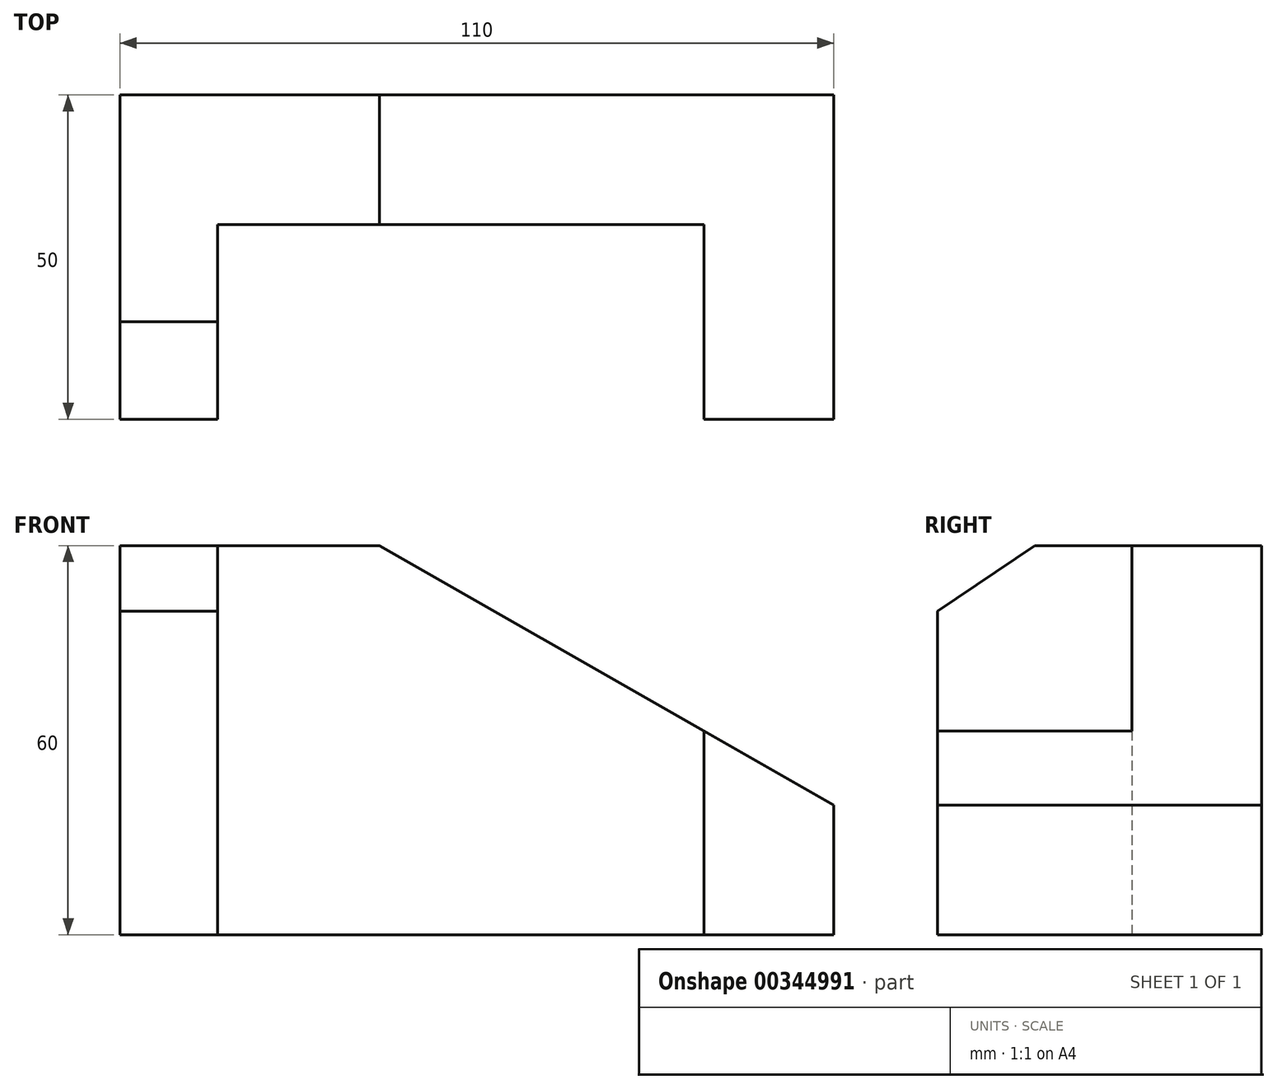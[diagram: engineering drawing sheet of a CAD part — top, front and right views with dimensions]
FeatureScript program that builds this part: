
annotation { "Feature Type Name" : "Feature", "Feature Type Description" : "" }
export const myFeature = defineFeature(function(context is Context, id is Id, definition is map)
    precondition{}
    {
        {
            var Q0;
            Q0=qCreatedBy(makeId("Top.planeOp"),FACE);
            var sketch = newSketch(context, id + "F0", { "sketchPlane" : qUnion([Q0])});
            skLineSegment(sketch, "E0.bottom", {"start": v(-55, 25) * mm, "end": v(55, 25) * mm});
            skLineSegment(sketch, "E0.top", {"start": v(-55, -25) * mm, "end": v(-40, -25) * mm});
            skLineSegment(sketch, "E0.left", {"start": v(-55, 25) * mm, "end": v(-55, -25) * mm});
            skLineSegment(sketch, "E0.right", {"start": v(55, 25) * mm, "end": v(55, -25) * mm});
            skPoint(sketch, "E0.middle", {"position": v(0, 0) * mm});
            skPoint(sketch, "E1", {"position": v(-15, 25) * mm});
            skPoint(sketch, "E2", {"position": v(-55, -5) * mm});
            skPoint(sketch, "E3", {"position": v(-40, 0) * mm});
            skPoint(sketch, "E4", {"position": v(35, -25) * mm});
            skLineSegment(sketch, "E5.trimOffspring", {"start": v(35, -25) * mm, "end": v(55, -25) * mm});
            skPoint(sketch, "E6", {"position": v(-55, 5) * mm});
            skLineSegment(sketch, "E7", {"start": v(-40, 5) * mm, "end": v(35, 5) * mm});
            skLineSegment(sketch, "E8", {"start": v(-40, -25) * mm, "end": v(-40, 5) * mm});
            skLineSegment(sketch, "E9", {"start": v(35, -25) * mm, "end": v(35, 5) * mm});
            skPoint(sketch, "E10.end.orphan", {"position": v(35, 0) * mm});
            skSolve(sketch);
        }
        {
            var Q0;
            Q0=makeQuery(id+"F0.imprint","IMPRINT",FACE,{"disambiguationData":[TD([[makeQuery(id+"F0.imprint","IMPRINT",EDGE,{"derivedFrom":sQuery(id+"F0.wireOp",EDGE,"E0.bottom")}),-1.0]])]});
            extrude(context, id + "F1", {"entities" : qUnion([Q0]), "depth" : 60 * mm});
        }
        {
            var Q0;
            Q0=makeQuery(id+"F1.opExtrude","SWEPT_FACE",FACE,{"disambiguationData":[OSD([sQuery(id+"F0.wireOp",EDGE,"E8")])]});
            var sketch = newSketch(context, id + "F2", { "sketchPlane" : qUnion([Q0])});
            skLineSegment(sketch, "E11.0", {"start": v(-25, 60) * mm, "end": v(5, 60) * mm});
            skLineSegment(sketch, "E11.1", {"start": v(-25, 60) * mm, "end": v(-25, 0) * mm});
            skLineSegment(sketch, "E11.2", {"start": v(5, 60) * mm, "end": v(5, 0) * mm});
            skLineSegment(sketch, "E11.3", {"start": v(-25, 0) * mm, "end": v(5, 0) * mm});
            skPoint(sketch, "E11.4", {"position": v(-10, 60) * mm});
            skPoint(sketch, "E12", {"position": v(-25, 49.9) * mm});
            skLineSegment(sketch, "E13", {"start": v(-25, 49.9) * mm, "end": v(-10, 60) * mm});
            skLineSegment(sketch, "E14", {"start": v(-25.07, 60.14) * mm, "end": v(-9.82, 60.17) * mm});
            skLineSegment(sketch, "E15", {"start": v(-25, 60) * mm, "end": v(-25, 49.9) * mm});
            skSolve(sketch);
        }
        {
            var Q0;
            {var subQ2=sQuery(id+"F2.wireOp",EDGE,"E13");Q0=makeQuery(id+"F2.imprint","IMPRINT",FACE,{"disambiguationData":[TD([[makeQuery(id+"F2.imprint","IMPRINT",EDGE,{"derivedFrom":subQ2}),1.0]])]});}
            extrude(context, id + "F3", {"entities" : qUnion([Q0]), "operationType" : NewBodyOperationType.REMOVE, "oppositeDirection" : true, "depth" : 15 * mm});
        }
        {
            var Q0;
            Q0=makeQuery(id+"F1.opExtrude","SWEPT_FACE",FACE,{"disambiguationData":[OSD([sQuery(id+"F0.wireOp",EDGE,"E0.bottom")])]});
            var sketch = newSketch(context, id + "F4", { "sketchPlane" : qUnion([Q0])});
            skLineSegment(sketch, "E16.0", {"start": v(55, 60) * mm, "end": v(-55, 60) * mm});
            skLineSegment(sketch, "E16.1", {"start": v(-55, 60) * mm, "end": v(-55, 0) * mm});
            skLineSegment(sketch, "E16.2", {"start": v(55, 0) * mm, "end": v(-55, 0) * mm});
            skLineSegment(sketch, "E16.3", {"start": v(55, 60) * mm, "end": v(55, 0) * mm});
            skPoint(sketch, "E17", {"position": v(15, 60) * mm});
            skPoint(sketch, "E18", {"position": v(-55, 20) * mm});
            skLineSegment(sketch, "E19", {"start": v(-55, 20) * mm, "end": v(15, 60) * mm});
            skSolve(sketch);
        }
        {
            var Q0;
            {var subQ3=sQuery(id+"F4.wireOp",EDGE,"E19");Q0=makeQuery(id+"F4.imprint","IMPRINT",FACE,{"disambiguationData":[TD([[makeQuery(id+"F4.imprint","IMPRINT",EDGE,{"derivedFrom":subQ3}),1.0]])]});}
            extrude(context, id + "F5", {"entities" : qUnion([Q0]), "operationType" : NewBodyOperationType.REMOVE, "oppositeDirection" : true, "depth" : 50 * mm});
        }
    });
